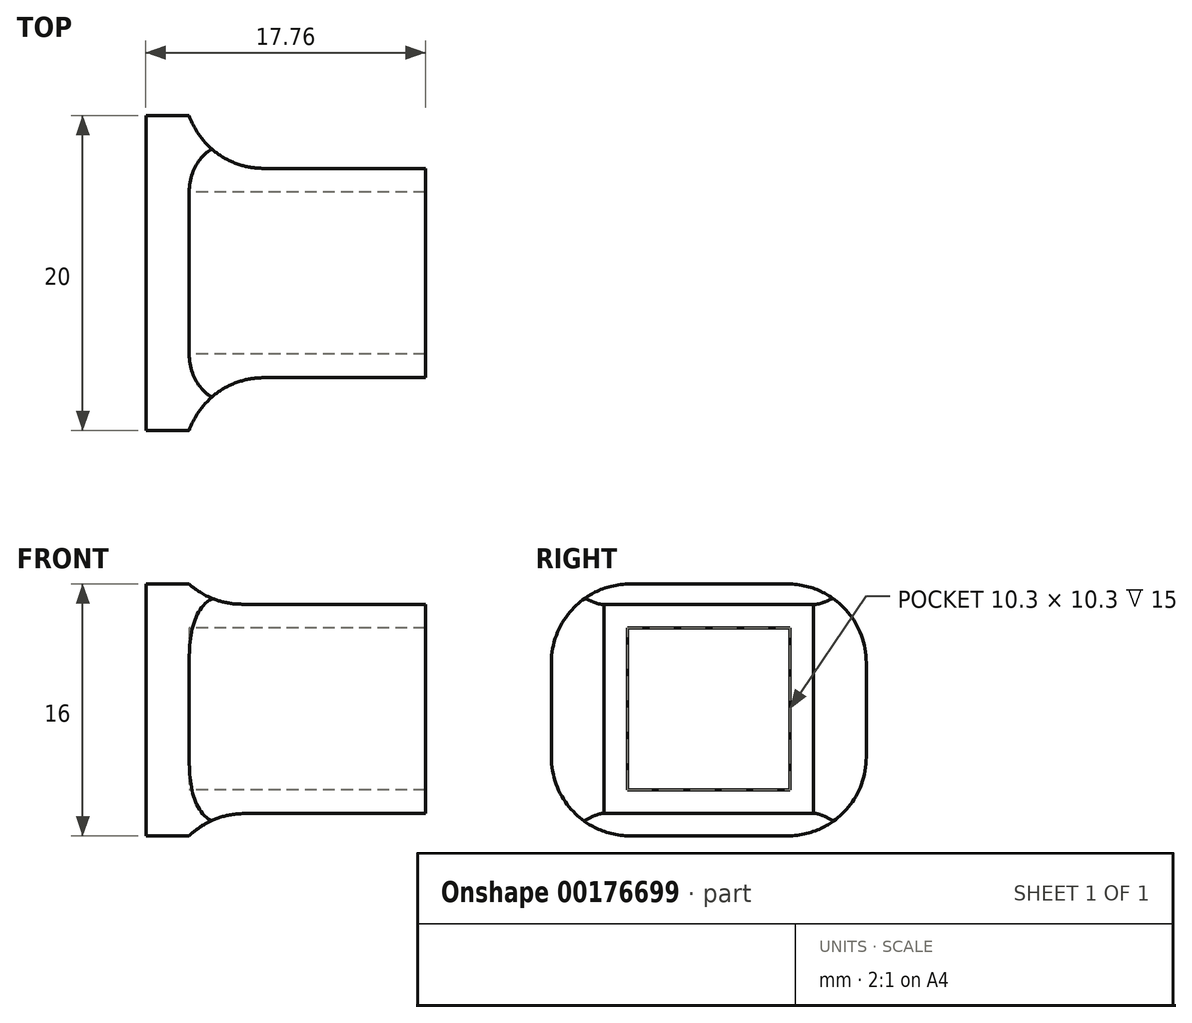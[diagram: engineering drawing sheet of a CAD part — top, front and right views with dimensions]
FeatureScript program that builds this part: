
annotation { "Feature Type Name" : "Feature", "Feature Type Description" : "" }
export const myFeature = defineFeature(function(context is Context, id is Id, definition is map)
    precondition{}
    {
        {
            var Q0;
            Q0=qCreatedBy(makeId("Top.planeOp"),FACE);
            var sketch = newSketch(context, id + "F0", { "sketchPlane" : qUnion([Q0])});
            skLineSegment(sketch, "E0.bottom", {"start": v(-1.37, 10) * mm, "end": v(1.38, 10) * mm});
            skLineSegment(sketch, "E0.top", {"start": v(-1.38, -10) * mm, "end": v(1.37, -10) * mm});
            skLineSegment(sketch, "E0.left", {"start": v(-1.37, 10) * mm, "end": v(-1.38, -10) * mm});
            skLineSegment(sketch, "E0.right", {"start": v(1.38, 10) * mm, "end": v(1.37, -10) * mm});
            skPoint(sketch, "E0.middle", {"position": v(0, 0) * mm});
            skSolve(sketch);
        }
        {
            var Q0;
            Q0=qSketchRegion(id+"F0",true);
            extrude(context, id + "F1", {"entities" : qUnion([Q0]), "depth" : 16 * mm});
        }
        {
            var Q0;
            Q0=makeQuery(id+"F1.opExtrude","SWEPT_FACE",FACE,{"disambiguationData":[OSD([sQuery(id+"F0.wireOp",EDGE,"E0.right")])]});
            var sketch = newSketch(context, id + "F2", { "sketchPlane" : qUnion([Q0])});
            skLineSegment(sketch, "E1.bottom", {"start": v(-10, 16) * mm, "end": v(10, 16) * mm});
            skLineSegment(sketch, "E1.top", {"start": v(-10, 0) * mm, "end": v(10, 0) * mm});
            skLineSegment(sketch, "E1.left", {"start": v(-10, 16) * mm, "end": v(-10, 0) * mm});
            skLineSegment(sketch, "E1.right", {"start": v(10, 16) * mm, "end": v(10, 0) * mm});
            skLineSegment(sketch, "E2.bottom", {"start": v(-5.15, 13.22) * mm, "end": v(5.15, 13.22) * mm});
            skLineSegment(sketch, "E2.top", {"start": v(-5.15, 2.92) * mm, "end": v(5.15, 2.92) * mm});
            skLineSegment(sketch, "E2.left", {"start": v(-5.15, 13.22) * mm, "end": v(-5.15, 2.92) * mm});
            skLineSegment(sketch, "E2.right", {"start": v(5.15, 13.22) * mm, "end": v(5.15, 2.92) * mm});
            skLineSegment(sketch, "E3.0", {"start": v(-6.65, 14.72) * mm, "end": v(6.65, 14.72) * mm});
            skLineSegment(sketch, "E3.1", {"start": v(-6.65, 14.72) * mm, "end": v(-6.65, 1.42) * mm});
            skLineSegment(sketch, "E3.2", {"start": v(-6.65, 1.42) * mm, "end": v(6.65, 1.42) * mm});
            skLineSegment(sketch, "E3.3", {"start": v(6.65, 14.72) * mm, "end": v(6.65, 1.42) * mm});
            skLineSegment(sketch, "E4", {"start": v(0, 0) * mm, "end": v(0, 16) * mm});
            skPoint(sketch, "E5", {"position": v(0, 8) * mm});
            skPoint(sketch, "E6.positionSnap0", {"position": v(0, 13.22) * mm});
            skPoint(sketch, "E7.positionSnap0", {"position": v(0, 16) * mm});
            skPoint(sketch, "E7.positionSnap1", {"position": v(10, 8) * mm});
            skSolve(sketch);
        }
        {
            var Q0;
            Q0=qSketchRegion(id+"F2",true);
            var Q1;
            Q1=makeQuery(id+"F2.imprint","IMPRINT",FACE,{"disambiguationData":[TD([[makeQuery(id+"F2.imprint","IMPRINT",EDGE,{"derivedFrom":sQuery(id+"F2.wireOp",EDGE,"E2.bottom")}),-1.0]])]});
            var Q2;
            Q2=makeQuery(id+"F2.imprint","IMPRINT",FACE,{"disambiguationData":[TD([[makeQuery(id+"F2.imprint","IMPRINT",EDGE,{"derivedFrom":sQuery(id+"F2.wireOp",EDGE,"E2.bottom")}),1.0]])]});
            var Q3;
            Q3=makeQuery(id+"F2.imprint","IMPRINT",FACE,{"disambiguationData":[TD([[makeQuery(id+"F2.imprint","IMPRINT",EDGE,{"derivedFrom":sQuery(id+"F2.wireOp",EDGE,"4b76e74c-1ac9-4312-af6a-232a9c3240f70.MirrorCS")}),-1.0]])]});
            var Q4;
            Q4=makeQuery(id+"F2.imprint","IMPRINT",FACE,{"disambiguationData":[TD([[makeQuery(id+"F2.imprint","IMPRINT",EDGE,{"derivedFrom":sQuery(id+"F2.wireOp",EDGE,"4b76e74c-1ac9-4312-af6a-232a9c3240f70.MirrorCS")}),1.0]])]});
            extrude(context, id + "F3", {"entities" : qUnion([Q0, Q1, Q2, Q3, Q4]), "operationType" : NewBodyOperationType.ADD, "oppositeDirection" : true, "depth" : 2.75 * mm});
        }
        {
            var Q0;
            Q0=makeQuery(id+"F2.imprint","IMPRINT",FACE,{"disambiguationData":[TD([[makeQuery(id+"F2.imprint","IMPRINT",EDGE,{"derivedFrom":sQuery(id+"F2.wireOp",EDGE,"E2.bottom")}),1.0]])]});
            var Q1;
            Q1=makeQuery(id+"F2.imprint","IMPRINT",FACE,{"disambiguationData":[TD([[makeQuery(id+"F2.imprint","IMPRINT",EDGE,{"derivedFrom":sQuery(id+"F2.wireOp",EDGE,"4b76e74c-1ac9-4312-af6a-232a9c3240f70.MirrorCS")}),-1.0]])]});
            extrude(context, id + "F4", {"entities" : qUnion([Q0, Q1]), "operationType" : NewBodyOperationType.ADD, "depth" : 15 * mm});
        }
        {
            var Q0;
            Q0=makeQuery(id+"F3.boolean.opBoolean","INTERSECT",EDGE,{"derivedFrom":[makeQuery(id+"F1.opExtrude","SWEPT_FACE",FACE,{"disambiguationData":[OSD([sQuery(id+"F0.wireOp",EDGE,"E0.bottom")])]}),makeQuery(id+"F3.opExtrude","CAP_FACE",FACE,{"disambiguationData":[OSD([sQuery(id+"F2.wireOp",EDGE,"E1.bottom"),sQuery(id+"F2.wireOp",EDGE,"E1.top"),sQuery(id+"F2.wireOp",EDGE,"E1.left"),sQuery(id+"F2.wireOp",EDGE,"E1.right")])],"isStart":false})]});
            var Q1;
            Q1=makeQuery(id+"F3.boolean.opBoolean","INTERSECT",EDGE,{"derivedFrom":[makeQuery(id+"F1.opExtrude","SWEPT_FACE",FACE,{"disambiguationData":[OSD([sQuery(id+"F0.wireOp",EDGE,"E0.top")])]}),makeQuery(id+"F3.opExtrude","CAP_FACE",FACE,{"disambiguationData":[OSD([sQuery(id+"F2.wireOp",EDGE,"E1.bottom"),sQuery(id+"F2.wireOp",EDGE,"E1.top"),sQuery(id+"F2.wireOp",EDGE,"E1.left"),sQuery(id+"F2.wireOp",EDGE,"E1.right")])],"isStart":false})]});
            var Q2;
            Q2=makeQuery(id+"F4.opExtrude","CAP_EDGE",EDGE,{"disambiguationData":[OSD([sQuery(id+"F2.wireOp",EDGE,"E3.0")])],"isStart":true});
            var Q3;
            Q3=makeQuery(id+"F4.opExtrude","CAP_EDGE",EDGE,{"disambiguationData":[OSD([sQuery(id+"F2.wireOp",EDGE,"E3.1")])],"isStart":true});
            var Q4;
            Q4=makeQuery(id+"F4.opExtrude","CAP_EDGE",EDGE,{"disambiguationData":[OSD([sQuery(id+"F2.wireOp",EDGE,"E3.3")])],"isStart":true});
            var Q5;
            Q5=makeQuery(id+"F4.opExtrude","CAP_EDGE",EDGE,{"disambiguationData":[OSD([sQuery(id+"F2.wireOp",EDGE,"E3.2")])],"isStart":true});
            fillet(context, id + "F5", {"entities" : qUnion([Q0, Q1, Q2, Q3, Q4, Q5]), "radius" : 5 * mm, "tangentPropagation" : true, "allowEdgeOverflow" : false});
        }
        {
            var Q0;
            Q0=makeQuery(id+"F1.opExtrude","CAP_EDGE",EDGE,{"disambiguationData":[OSD([sQuery(id+"F0.wireOp",EDGE,"E0.top")])],"isStart":true});
            var Q1;
            Q1=makeQuery(id+"F1.opExtrude","CAP_EDGE",EDGE,{"disambiguationData":[OSD([sQuery(id+"F0.wireOp",EDGE,"E0.top")])],"isStart":false});
            var Q2;
            Q2=makeQuery(id+"F1.opExtrude","CAP_EDGE",EDGE,{"disambiguationData":[OSD([sQuery(id+"F0.wireOp",EDGE,"E0.bottom")])],"isStart":false});
            var Q3;
            Q3=makeQuery(id+"F1.opExtrude","CAP_EDGE",EDGE,{"disambiguationData":[OSD([sQuery(id+"F0.wireOp",EDGE,"E0.bottom")])],"isStart":true});
            fillet(context, id + "F6", {"entities" : qUnion([Q0, Q1, Q2, Q3]), "radius" : 5 * mm, "tangentPropagation" : true, "allowEdgeOverflow" : false});
        }
    });
